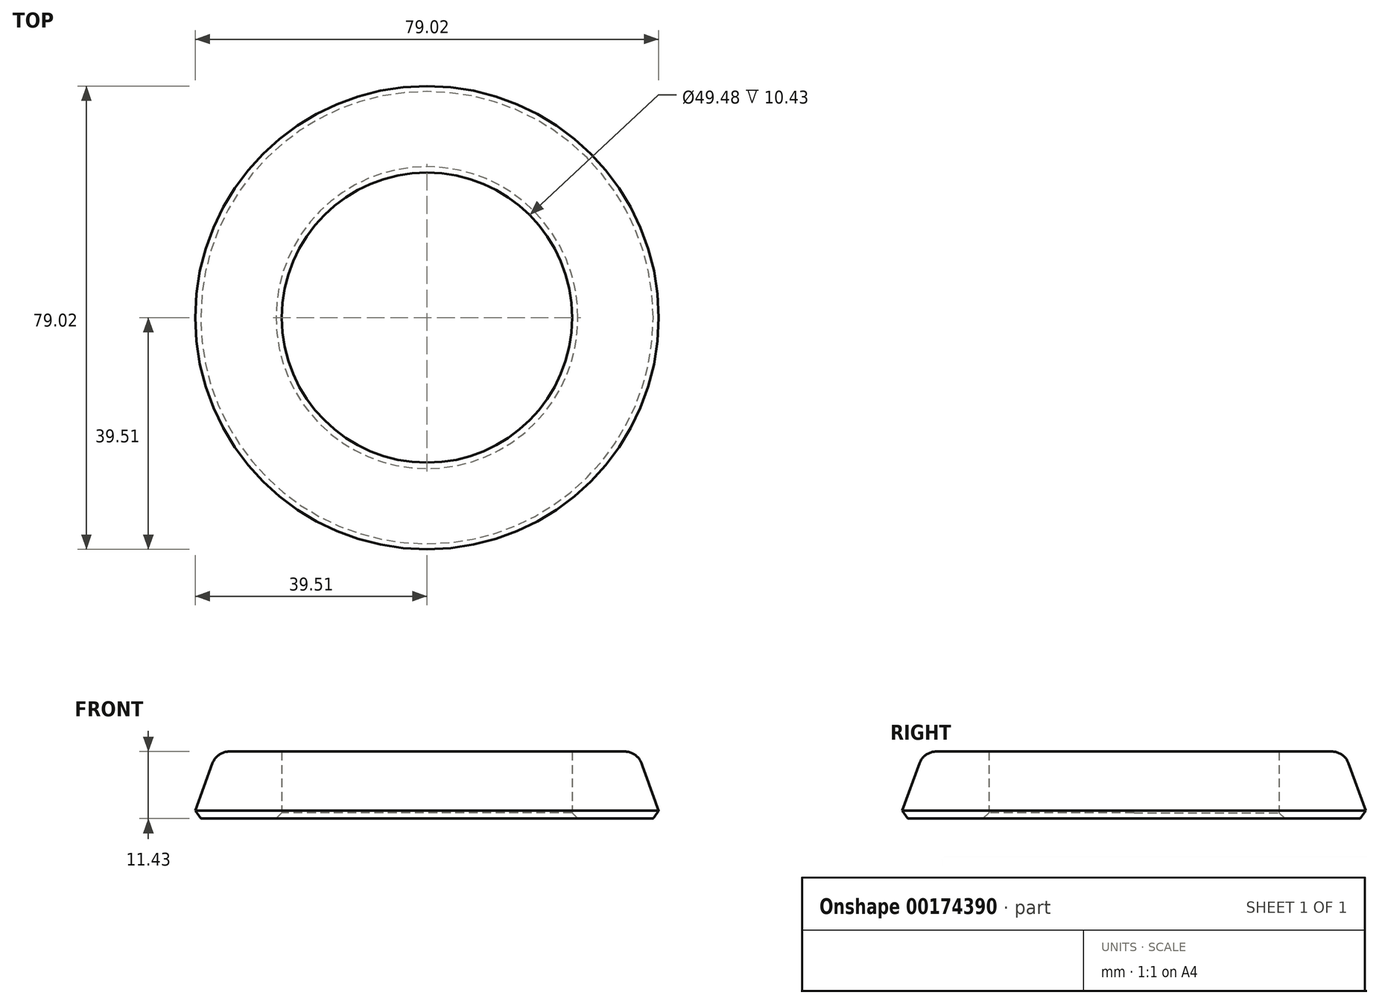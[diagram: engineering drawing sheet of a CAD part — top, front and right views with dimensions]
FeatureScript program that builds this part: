
annotation { "Feature Type Name" : "Feature", "Feature Type Description" : "" }
export const myFeature = defineFeature(function(context is Context, id is Id, definition is map)
    precondition{}
    {
        {
            var Q0;
            Q0=qCreatedBy(makeId("Top.planeOp"),FACE);
            var sketch = newSketch(context, id + "F0", { "sketchPlane" : qUnion([Q0])});
            skCircle(sketch, "E0", {"center": v(0, 0) * mm, "radius": 40 * mm});
            skSolve(sketch);
        }
        {
            var Q0;
            Q0=qCreatedBy(makeId("Front.planeOp"),FACE);
            var sketch = newSketch(context, id + "F1", { "sketchPlane" : qUnion([Q0])});
            skLineSegment(sketch, "E1", {"start": v(35.84, 11.43) * mm, "end": v(40, 0) * mm});
            skLineSegment(sketch, "E2", {"start": v(40, 0) * mm, "end": v(24.74, 0) * mm});
            skLineSegment(sketch, "E3", {"start": v(24.74, 0) * mm, "end": v(24.74, 11.43) * mm});
            skLineSegment(sketch, "E4", {"start": v(24.74, 11.43) * mm, "end": v(35.84, 11.43) * mm});
            skSolve(sketch);
        }
        {
            var Q0;
            Q0=makeQuery(id+"F1.imprint","IMPRINT",FACE,{"disambiguationData":[TD([[makeQuery(id+"F1.imprint","IMPRINT",EDGE,{"derivedFrom":sQuery(id+"F1.wireOp",EDGE,"E1")}),-1.0]])]});
            var Q1;
            Q1=sQuery(id+"F0.wireOp",EDGE,"E0");
            revolve(context, id + "F2", {"entities" : qUnion([Q0]), "axis" : qUnion([Q1]), "revolveType" : RevolveType.FULL});
        }
        {
            var Q0;
            Q0=makeQuery(id+"F2.opRevolve","SWEPT_EDGE",EDGE,{"disambiguationData":[OSD([sQuery(id+"F1.wireOp",EDGE,"E1"),sQuery(id+"F1.wireOp",EDGE,"E4")])]});
            fillet(context, id + "F3", {"entities" : qUnion([Q0]), "radius" : 3 * mm, "tangentPropagation" : true, "allowEdgeOverflow" : false});
        }
        {
            var Q0;
            Q0=makeQuery(id+"F2.opRevolve","SWEPT_EDGE",EDGE,{"disambiguationData":[OSD([sQuery(id+"F1.wireOp",EDGE,"E1"),sQuery(id+"F1.wireOp",EDGE,"E2")])]});
            var Q1;
            Q1=makeQuery(id+"F2.opRevolve","SWEPT_EDGE",EDGE,{"disambiguationData":[OSD([sQuery(id+"F1.wireOp",EDGE,"E2"),sQuery(id+"F1.wireOp",EDGE,"E3")])]});
            chamfer(context, id + "F4", {"entities" : qUnion([Q0, Q1]), "width" : 1 * mm, "tangentPropagation" : true});
        }
    });
